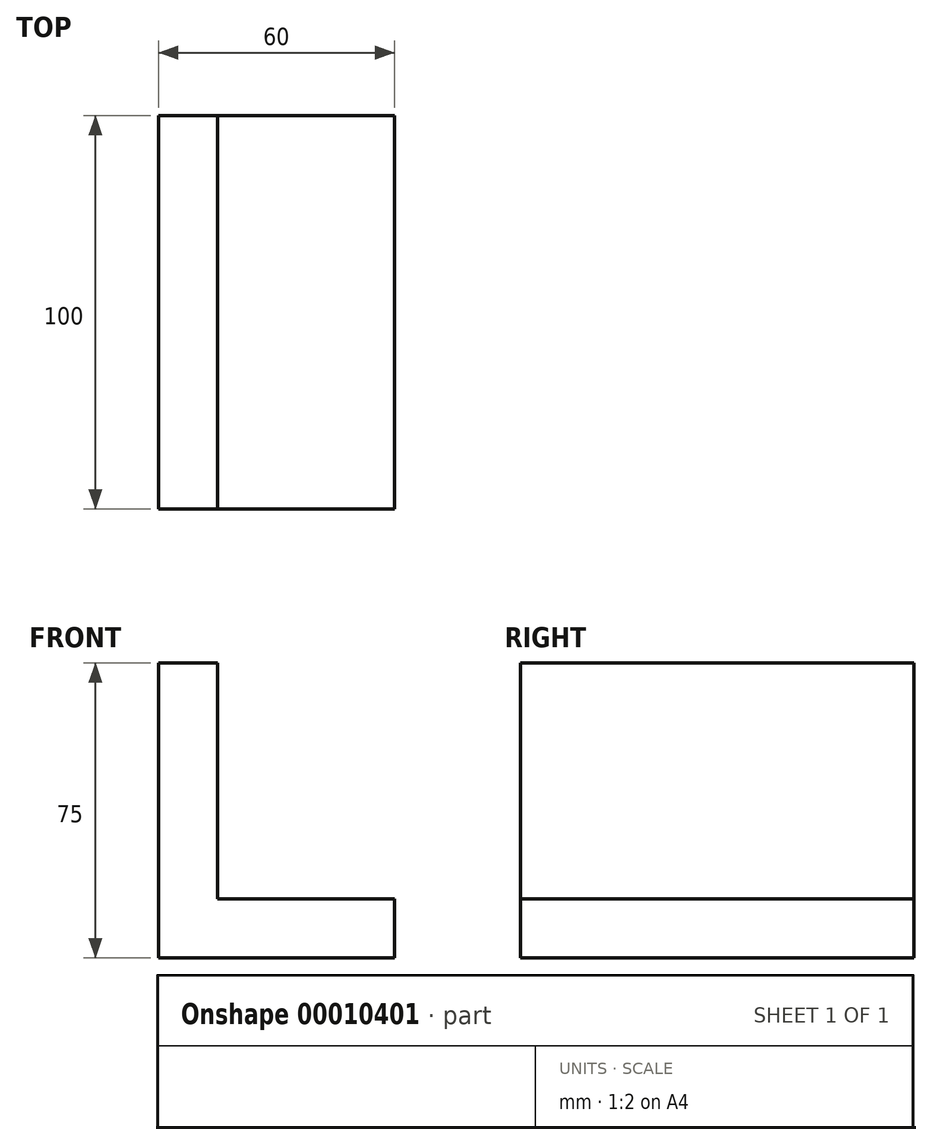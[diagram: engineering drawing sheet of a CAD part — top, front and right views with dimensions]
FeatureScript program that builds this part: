
annotation { "Feature Type Name" : "Feature", "Feature Type Description" : "" }
export const myFeature = defineFeature(function(context is Context, id is Id, definition is map)
    precondition{}
    {
        {
            var Q0;
            Q0=qCreatedBy(makeId("Front.planeOp"),FACE);
            var sketch = newSketch(context, id + "F0", { "sketchPlane" : qUnion([Q0])});
            skLineSegment(sketch, "E0", {"start": v(0, 0) * mm, "end": v(60, 0) * mm});
            skLineSegment(sketch, "E1", {"start": v(60, 0) * mm, "end": v(60, 15) * mm});
            skLineSegment(sketch, "E2", {"start": v(60, 15) * mm, "end": v(15, 15) * mm});
            skLineSegment(sketch, "E3", {"start": v(15, 15) * mm, "end": v(15, 75) * mm});
            skLineSegment(sketch, "E4", {"start": v(15, 75) * mm, "end": v(0, 75) * mm});
            skLineSegment(sketch, "E5", {"start": v(0, 75) * mm, "end": v(0, 0) * mm});
            skSolve(sketch);
        }
        {
            var Q0;
            Q0 = qSketchRegion(id + "F0", true);
            extrude(context, id + "F1", {"entities" : qUnion([Q0]), "oppositeDirection" : true, "depth" : 100 * mm});
        }
    });
